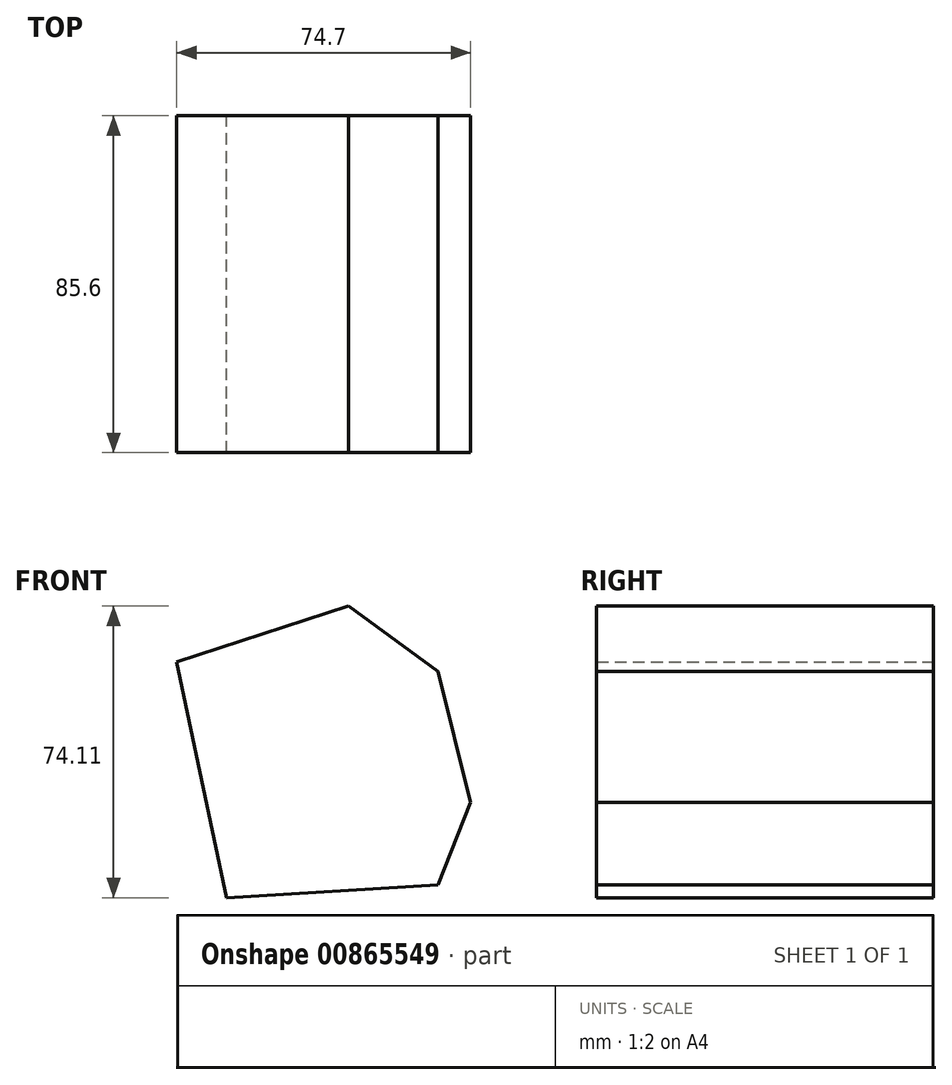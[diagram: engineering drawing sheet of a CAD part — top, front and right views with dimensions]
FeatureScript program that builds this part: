
annotation { "Feature Type Name" : "Feature", "Feature Type Description" : "" }
export const myFeature = defineFeature(function(context is Context, id is Id, definition is map)
    precondition{}
    {
        {
            var Q0;
            Q0=qCreatedBy(makeId("Front.planeOp"),FACE);
            var sketch = newSketch(context, id + "F0", { "sketchPlane" : qUnion([Q0])});
            skLineSegment(sketch, "E0", {"start": v(-31.52, 32.85) * mm, "end": v(12.18, 47.02) * mm});
            skLineSegment(sketch, "E1", {"start": v(12.18, 47.02) * mm, "end": v(34.91, 30.48) * mm});
            skLineSegment(sketch, "E2", {"start": v(34.91, 30.48) * mm, "end": v(43.18, -2.88) * mm});
            skLineSegment(sketch, "E3", {"start": v(43.18, -2.88) * mm, "end": v(34.91, -23.84) * mm});
            skLineSegment(sketch, "E4", {"start": v(34.91, -23.84) * mm, "end": v(-18.82, -27.09) * mm});
            skLineSegment(sketch, "E5", {"start": v(-18.82, -27.09) * mm, "end": v(-31.52, 32.85) * mm});
            skSolve(sketch);
        }
        {
            var Q0;
            Q0=makeQuery(id+"F0.imprint","IMPRINT",FACE,{"disambiguationData":[TD([[makeQuery(id+"F0.imprint","IMPRINT",EDGE,{"derivedFrom":sQuery(id+"F0.wireOp",EDGE,"E0")}),-1.0]])]});
            extrude(context, id + "F1", {"entities" : qUnion([Q0]), "depth" : 85.6 * mm, "offsetDistance" : 25.4 * mm});
        }
    });
